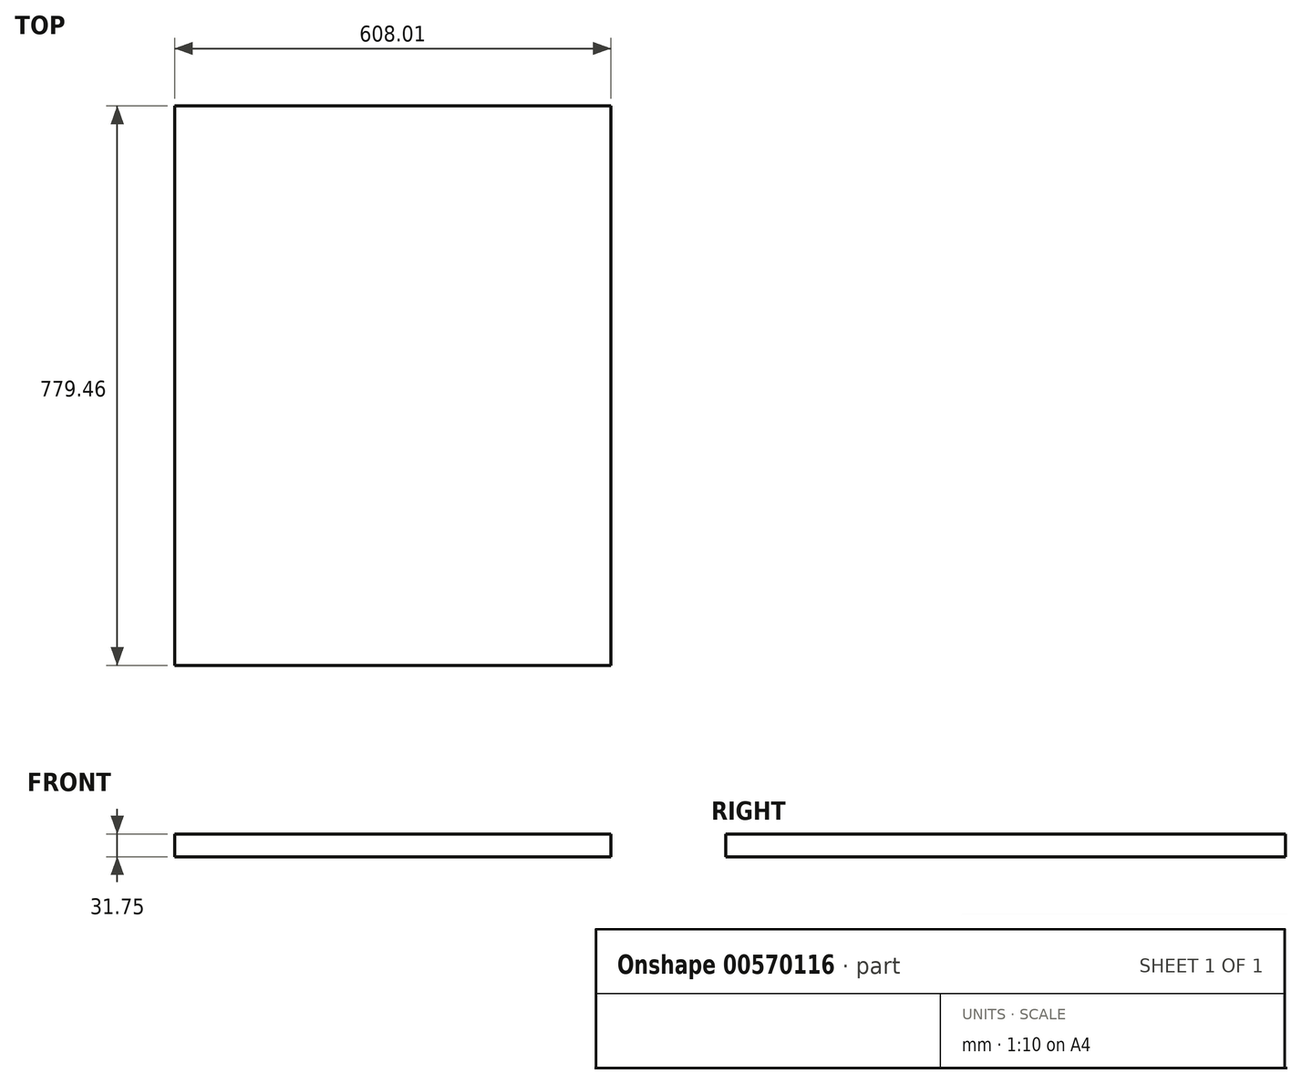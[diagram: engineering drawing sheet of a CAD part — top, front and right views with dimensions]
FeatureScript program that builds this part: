
annotation { "Feature Type Name" : "Feature", "Feature Type Description" : "" }
export const myFeature = defineFeature(function(context is Context, id is Id, definition is map)
    precondition{}
    {
        {
            var Q0;
            Q0=qCreatedBy(makeId("Front.planeOp"),FACE);
            var sketch = newSketch(context, id + "F0", { "sketchPlane" : qUnion([Q0])});
            skLineSegment(sketch, "E0.bottom", {"start": v(0, 0) * mm, "end": v(608.01, 0) * mm});
            skLineSegment(sketch, "E0.top", {"start": v(0, -31.75) * mm, "end": v(608.01, -31.75) * mm});
            skLineSegment(sketch, "E0.left", {"start": v(0, 0) * mm, "end": v(0, -31.75) * mm});
            skLineSegment(sketch, "E0.right", {"start": v(608.01, 0) * mm, "end": v(608.01, -31.75) * mm});
            skSolve(sketch);
        }
        {
            var Q0;
            Q0=makeQuery(id+"F0.imprint","IMPRINT",FACE,{"disambiguationData":[TD([[makeQuery(id+"F0.imprint","IMPRINT",EDGE,{"derivedFrom":sQuery(id+"F0.wireOp",EDGE,"E0.bottom")}),-1.0]])]});
            extrude(context, id + "F1", {"entities" : qUnion([Q0]), "depth" : 779.46 * mm, "offsetDistance" : 25.4 * mm});
        }
    });
